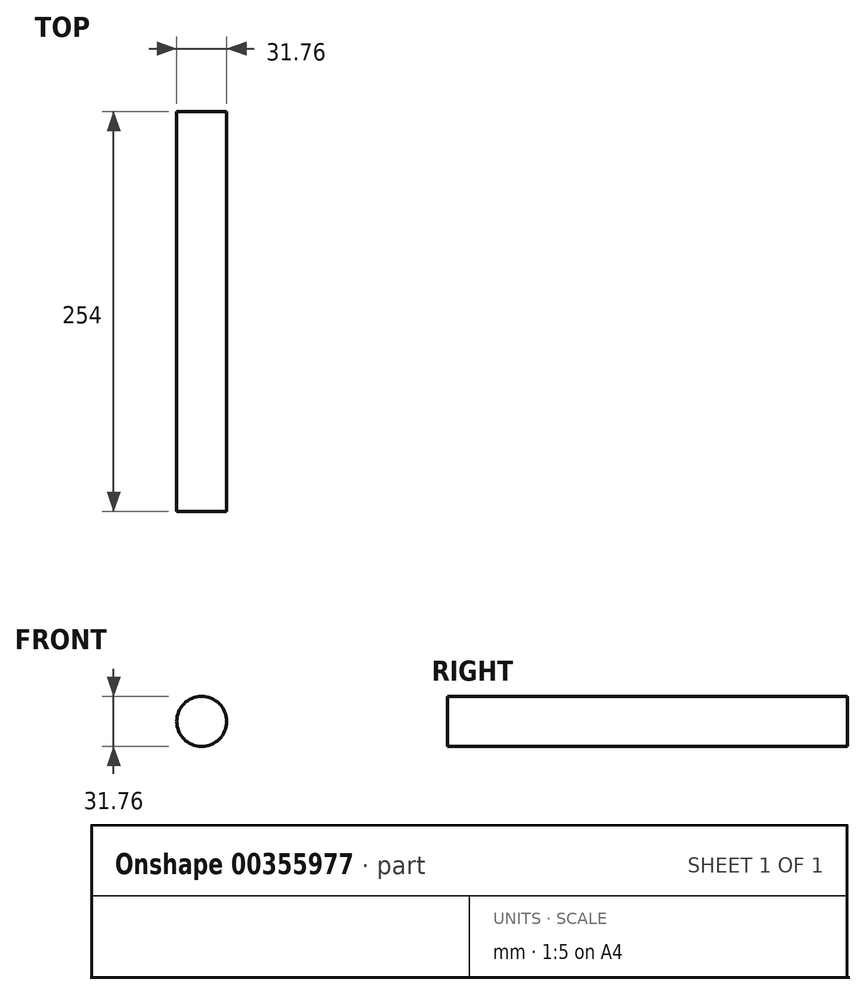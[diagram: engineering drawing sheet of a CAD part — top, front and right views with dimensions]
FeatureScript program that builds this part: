
annotation { "Feature Type Name" : "Feature", "Feature Type Description" : "" }
export const myFeature = defineFeature(function(context is Context, id is Id, definition is map)
    precondition{}
    {
        {
            var Q0;
            Q0=qCreatedBy(makeId("Front.planeOp"),FACE);
            var sketch = newSketch(context, id + "F0", { "sketchPlane" : qUnion([Q0])});
            skCircle(sketch, "E0", {"center": v(0, 0) * mm, "radius": 15.88 * mm});
            skSolve(sketch);
        }
        {
            var Q0;
            Q0=qSketchRegion(id+"F0",true);
            extrude(context, id + "F1", {"entities" : qUnion([Q0]), "depth" : 254 * mm});
        }
    });
